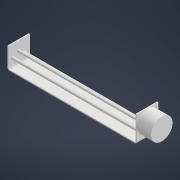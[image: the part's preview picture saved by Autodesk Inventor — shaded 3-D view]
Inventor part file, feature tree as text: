
AUTODESK INVENTOR PART (.ipt)
format: ipt  version: 2022 (Build 260153000, 153)  size: 155,648 bytes
history: native  units: mm
features: sheet_metal_op x7, sketch x5, other x3, extrude x2
ambient origin geometry x8: Origin, YZ Plane, XZ Plane, XY Plane, X Axis, Y Axis, Z Axis, Center Point
bodies: Solid1 (feature_tree)
feature tree (17):
  sheet_metal_op  "Face1"
  sheet_metal_op  "Flange1"
  sheet_metal_op  "Flange2"
  extrude  "Extrusion1"  Depth=15.0mm
  extrude  "Extrusion2"  Depth=0.75mm
  sketch  "Sketch1"  dims[d0=90.0mm d1=15.0mm]
  other  "Plate1"
  sketch  "Sketch2"  dims[d2=0.75mm d3=0.75mm]
  other  "Plate2"
  sheet_metal_op  "Bend1"
  sheet_metal_op  "Corner1"
  sketch  "Sketch3"  dims[d4=0.375mm]
  other  "Plate3"
  sheet_metal_op  "Bend2"
  sheet_metal_op  "Corner2"
  sketch  "Sketch4"  dims[d5=1.5mm]
  sketch  "Sketch5"  dims[d6=0.75mm d7=14.5mm d8=90.0deg d9=0.75mm d10=3.0mm d11=0.75mm d12=0.75mm d13=0.75mm d14=0.375mm d15=1.5mm d16=0.75mm d17=18.0mm d18=90.0deg d19=0.75mm d20=3.0mm d21=0.75mm d22=0.75mm d23=10.5mm d24=15.0mm d25=10.0mm d26=0.0mm d27=10.0mm d28=0.0mm d29=10.5mm d30=3.0mm d31=3.0mm d32=3.0mm d33=5.0mm d34=5.0mm d35=4.0mm]
